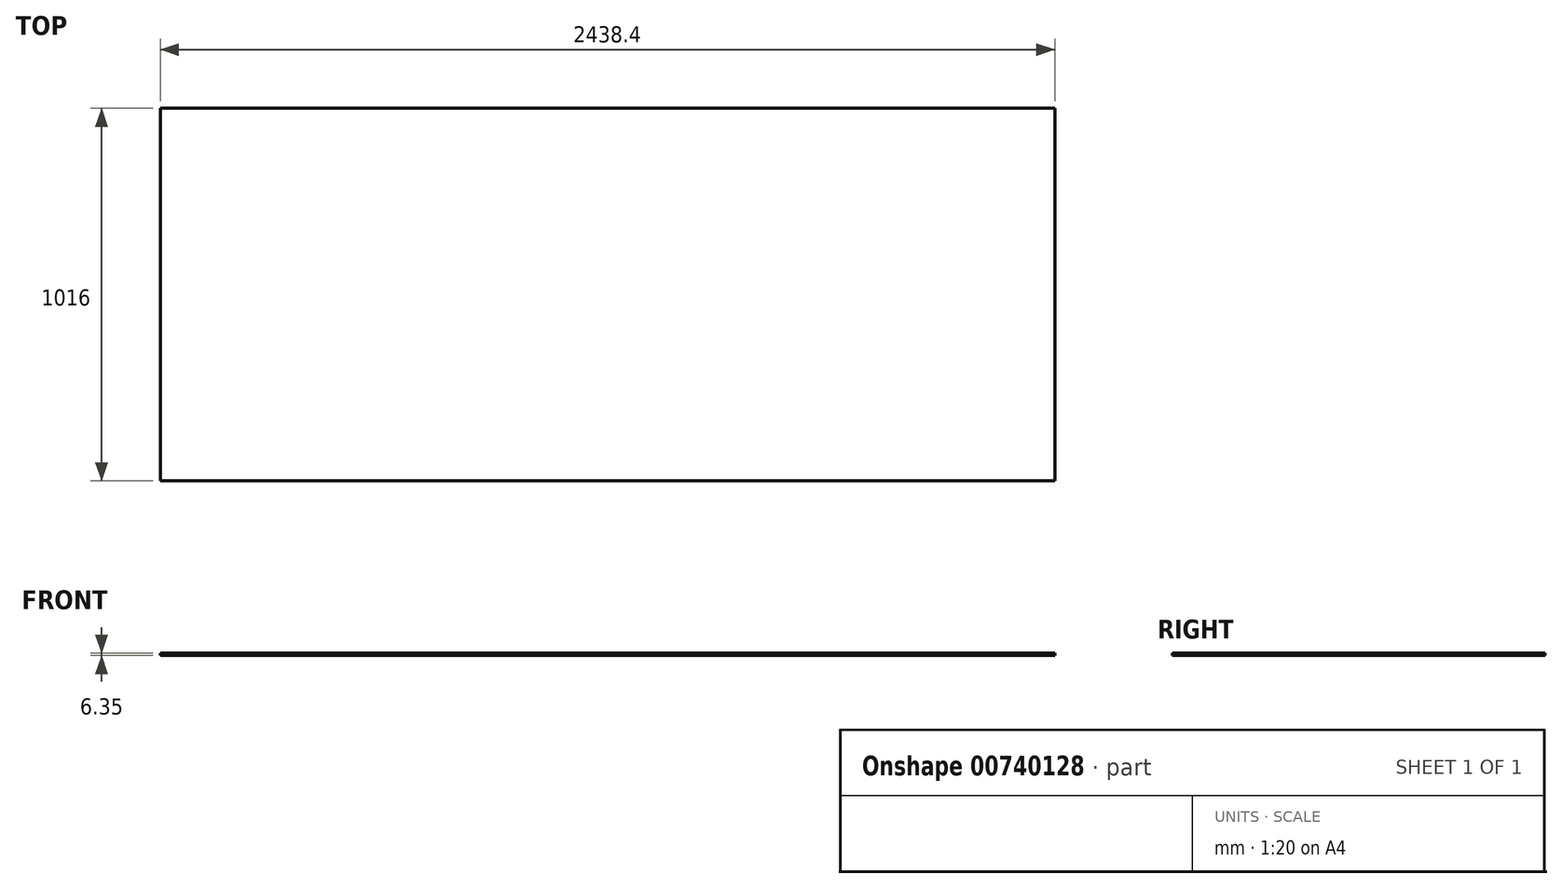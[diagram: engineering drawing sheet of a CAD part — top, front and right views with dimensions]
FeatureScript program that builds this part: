
annotation { "Feature Type Name" : "Feature", "Feature Type Description" : "" }
export const myFeature = defineFeature(function(context is Context, id is Id, definition is map)
    precondition{}
    {
        {
            var Q0;
            Q0=qCreatedBy(makeId("Top.planeOp"),FACE);
            var sketch = newSketch(context, id + "F0", { "sketchPlane" : qUnion([Q0])});
            skLineSegment(sketch, "E0.bottom", {"start": v(2460.7, -203.66) * mm, "end": v(22.3, -203.66) * mm});
            skLineSegment(sketch, "E0.top", {"start": v(2460.7, 812.34) * mm, "end": v(22.3, 812.34) * mm});
            skLineSegment(sketch, "E0.left", {"start": v(2460.7, -203.66) * mm, "end": v(2460.7, 812.34) * mm});
            skLineSegment(sketch, "E0.right", {"start": v(22.3, -203.66) * mm, "end": v(22.3, 812.34) * mm});
            skSolve(sketch);
        }
        {
            var Q0;
            Q0=makeQuery(id+"F0.imprint","IMPRINT",FACE,{"disambiguationData":[TD([[makeQuery(id+"F0.imprint","IMPRINT",EDGE,{"derivedFrom":sQuery(id+"F0.wireOp",EDGE,"E0.right")}),1.0]])]});
            var Q1;
            Q1=makeQuery(id+"F0.imprint","IMPRINT",FACE,{"disambiguationData":[TD([[makeQuery(id+"F0.imprint","IMPRINT",EDGE,{"derivedFrom":sQuery(id+"F0.wireOp",EDGE,"E0.bottom")}),-1.0]])]});
            extrude(context, id + "F1", {"entities" : qUnion([Q0, Q1]), "depth" : 6.35 * mm, "offsetDistance" : 25.4 * mm});
        }
    });
